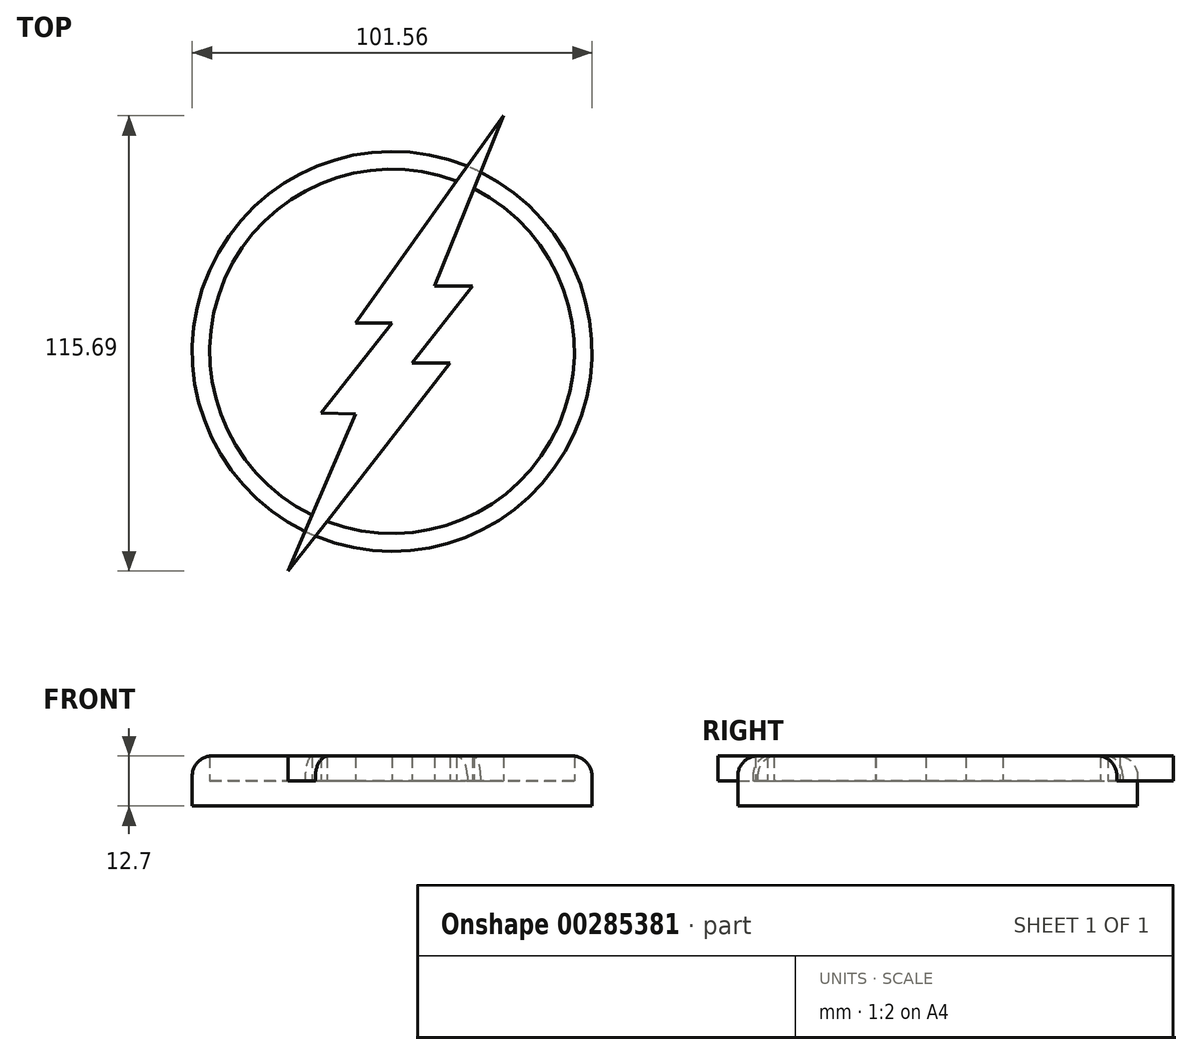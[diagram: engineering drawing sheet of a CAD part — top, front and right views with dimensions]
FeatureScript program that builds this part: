
annotation { "Feature Type Name" : "Feature", "Feature Type Description" : "" }
export const myFeature = defineFeature(function(context is Context, id is Id, definition is map)
    precondition{}
    {
        {
            var Q0;
            Q0=qCreatedBy(makeId("Top.planeOp"),FACE);
            var sketch = newSketch(context, id + "F0", { "sketchPlane" : qUnion([Q0])});
            skCircle(sketch, "E0", {"center": v(0, 0) * mm, "radius": 50.78 * mm});
            skCircle(sketch, "E1", {"center": v(0, 0) * mm, "radius": 46.3 * mm});
            skSolve(sketch);
        }
        {
            var Q0;
            Q0=makeQuery(id+"F0.imprint","IMPRINT",FACE,{"disambiguationData":[TD([[makeQuery(id+"F0.imprint","IMPRINT",EDGE,{"derivedFrom":sQuery(id+"F0.wireOp",EDGE,"E1")}),1.0]])]});
            extrude(context, id + "F1", {"entities" : qUnion([Q0]), "depth" : 6.35 * mm});
        }
        {
            var Q0;
            Q0 = qSketchRegion(id + "F0", true);
            extrude(context, id + "F2", {"entities" : qUnion([Q0]), "operationType" : NewBodyOperationType.ADD, "depth" : 12.7 * mm});
        }
        {
            var Q0;
            Q0=makeQuery(id+"F2.opExtrude","CAP_EDGE",EDGE,{"disambiguationData":[OSD([sQuery(id+"F0.wireOp",EDGE,"E0")])],"isStart":false});
            fillet(context, id + "F3", {"entities" : qUnion([Q0]), "radius" : 5.08 * mm, "tangentPropagation" : true, "allowEdgeOverflow" : false});
        }
        {
            var Q0;
            Q0=makeQuery(id+"F1.opExtrude","CAP_FACE",FACE,{"disambiguationData":[OSD([sQuery(id+"F0.wireOp",EDGE,"E1")])],"isStart":false});
            var sketch = newSketch(context, id + "F4", { "sketchPlane" : qUnion([Q0])});
            skLineSegment(sketch, "E2", {"start": v(-26.37, -55.83) * mm, "end": v(14.74, -3) * mm});
            skLineSegment(sketch, "E3", {"start": v(14.74, -3) * mm, "end": v(5.11, -3) * mm});
            skLineSegment(sketch, "E4", {"start": v(5.11, -3) * mm, "end": v(20.4, 16.65) * mm});
            skLineSegment(sketch, "E5", {"start": v(20.4, 16.65) * mm, "end": v(10.83, 16.65) * mm});
            skLineSegment(sketch, "E6", {"start": v(10.83, 16.65) * mm, "end": v(28.27, 59.86) * mm});
            skLineSegment(sketch, "E7", {"start": v(-26.37, -55.83) * mm, "end": v(-9.32, -15.86) * mm});
            skLineSegment(sketch, "E8", {"start": v(-9.32, -15.86) * mm, "end": v(-18.05, -15.64) * mm});
            skLineSegment(sketch, "E9", {"start": v(-18.05, -15.64) * mm, "end": v(0, 7.22) * mm});
            skLineSegment(sketch, "E10", {"start": v(-9.32, 7.22) * mm, "end": v(28.27, 59.86) * mm});
            skLineSegment(sketch, "E11", {"start": v(-9.32, 7.22) * mm, "end": v(0, 7.22) * mm});
            skSolve(sketch);
        }
        {
            var Q0;
            Q0 = qSketchRegion(id + "F4", true);
            extrude(context, id + "F5", {"entities" : qUnion([Q0]), "operationType" : NewBodyOperationType.ADD, "depth" : 6.35 * mm});
        }
    });
